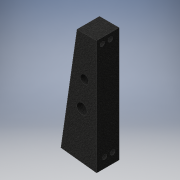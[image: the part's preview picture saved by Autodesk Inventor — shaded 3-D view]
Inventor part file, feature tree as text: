
AUTODESK INVENTOR PART (.ipt)
format: ipt  version: 2016 (Build 200138000, 138)  size: 151,040 bytes
history: native  units: in
note: dims shown in document units (in); Inventor stores cm internally (conversion verified against a paired STEP export)
features: extrude x3, sketch x3
ambient origin geometry x8: Origin, YZ Plane, XZ Plane, XY Plane, X Axis, Y Axis, Z Axis, Center Point
bodies: Solid1 (feature_tree)
feature tree (6):
  extrude  "Extrusion1"  Depth=2.4409in
  extrude  "Extrusion2"  Depth=0.2756in
  extrude  "Extrusion3"  Depth=1.5354in
  sketch  "Sketch1"  dims[d0=7.8346in d1=2.4409in]
  sketch  "Sketch2"  dims[d2=1.3386in d3=0.2756in]
  sketch  "Sketch3"  dims[d4=1.5354in d5=0.0in d6=0.315in d7=0.315in d8=0.5512in d9=0.5512in d10=6.7717in d11=0.315in d12=0.315in d13=0.5512in d14=0.3937in d16=1.5354in d17=0.0in d18=0.3937in d19=0.7087in d20=0.5906in d21=1.0039in d22=0.8268in d23=2.7165in d24=4.5354in d25=1.5354in d26=0.0in]
